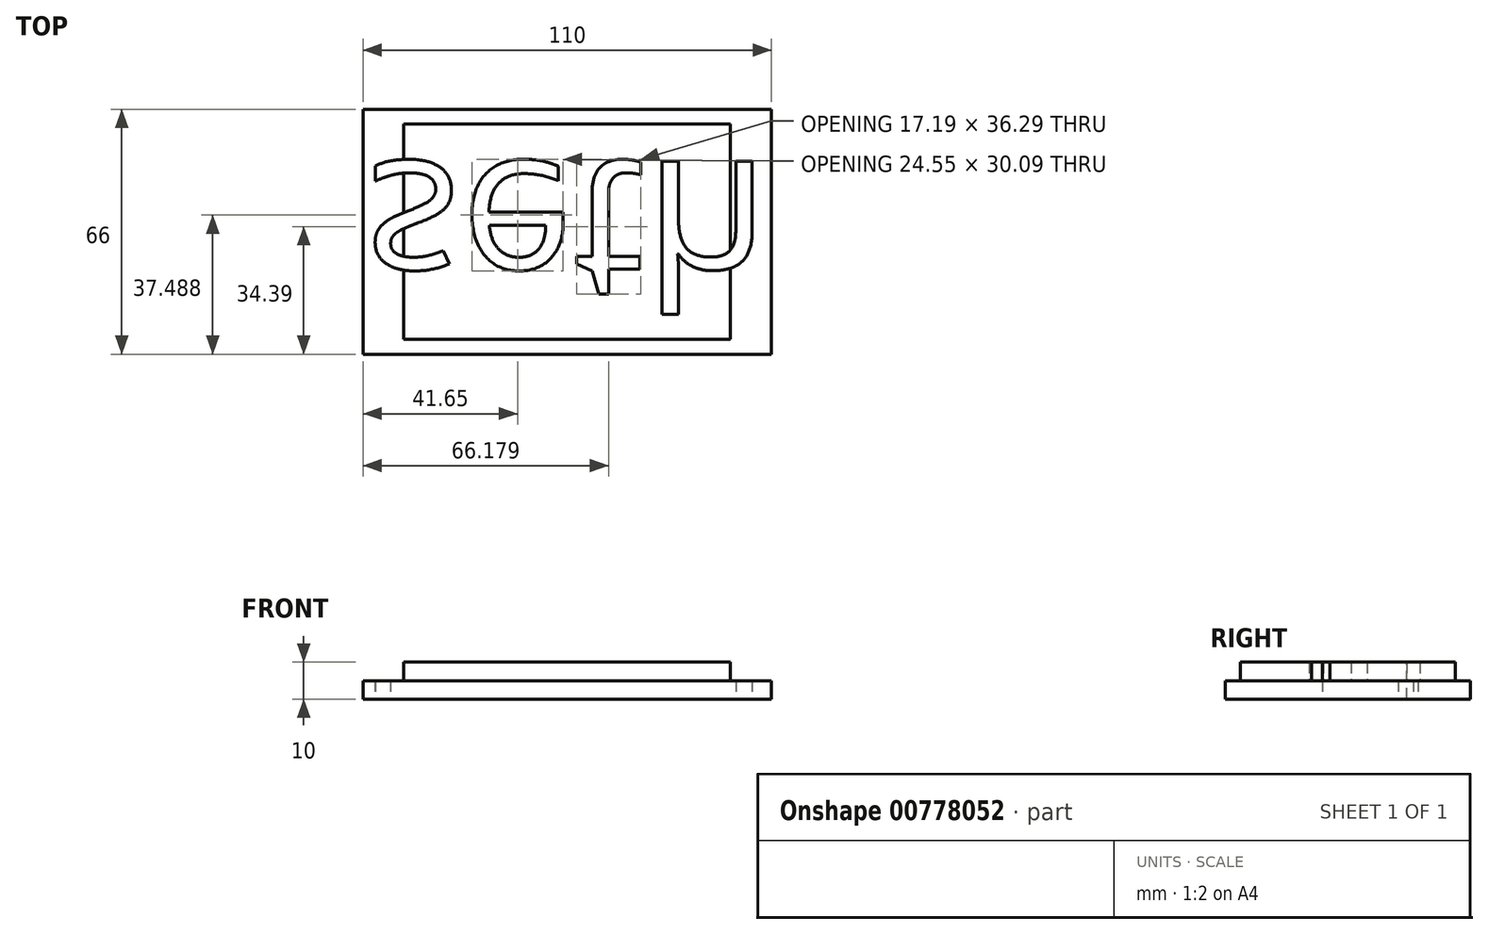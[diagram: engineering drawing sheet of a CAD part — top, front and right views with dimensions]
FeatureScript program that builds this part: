
annotation { "Feature Type Name" : "Feature", "Feature Type Description" : "" }
export const myFeature = defineFeature(function(context is Context, id is Id, definition is map)
    precondition{}
    {
        {
            var Q0;
            Q0=qCreatedBy(makeId("Top.planeOp"),FACE);
            var sketch = newSketch(context, id + "F0", { "sketchPlane" : qUnion([Q0])});
            skLineSegment(sketch, "E0.bottom", {"start": v(55, 33) * mm, "end": v(-55, 33) * mm});
            skLineSegment(sketch, "E0.top", {"start": v(55, -33) * mm, "end": v(-55, -33) * mm});
            skLineSegment(sketch, "E0.left", {"start": v(55, 33) * mm, "end": v(55, -33) * mm});
            skLineSegment(sketch, "E0.right", {"start": v(-55, 33) * mm, "end": v(-55, -33) * mm});
            skPoint(sketch, "E0.middle", {"position": v(0, 0) * mm});
            skSolve(sketch);
        }
        {
            var Q0;
            Q0=makeQuery(id+"F0.imprint","IMPRINT",FACE,{"disambiguationData":[TD([[makeQuery(id+"F0.imprint","IMPRINT",EDGE,{"derivedFrom":sQuery(id+"F0.wireOp",EDGE,"E0.bottom")}),1.0]])]});
            extrude(context, id + "F1", {"entities" : qUnion([Q0]), "depth" : 5 * mm, "offsetDistance" : 25 * mm});
        }
        {
            var Q0;
            Q0=makeQuery(id+"F1.opExtrude","CAP_FACE",FACE,{"disambiguationData":[OSD([sQuery(id+"F0.wireOp",EDGE,"E0.bottom"),sQuery(id+"F0.wireOp",EDGE,"E0.top"),sQuery(id+"F0.wireOp",EDGE,"E0.left"),sQuery(id+"F0.wireOp",EDGE,"E0.right")])],"isStart":false});
            var sketch = newSketch(context, id + "F2", { "sketchPlane" : qUnion([Q0])});
            skLineSegment(sketch, "E1.bottom", {"start": v(44, 29) * mm, "end": v(-44, 29) * mm});
            skLineSegment(sketch, "E1.top", {"start": v(44, -29) * mm, "end": v(-44, -29) * mm});
            skLineSegment(sketch, "E1.left", {"start": v(44, 29) * mm, "end": v(44, -29) * mm});
            skLineSegment(sketch, "E1.right", {"start": v(-44, 29) * mm, "end": v(-44, -29) * mm});
            skPoint(sketch, "E1.middle", {"position": v(0, 0) * mm});
            skSolve(sketch);
        }
        {
            var Q0;
            Q0=makeQuery(id+"F2.imprint","IMPRINT",FACE,{"disambiguationData":[TD([[makeQuery(id+"F2.imprint","IMPRINT",EDGE,{"derivedFrom":sQuery(id+"F2.wireOp",EDGE,"E1.bottom")}),1.0]])]});
            extrude(context, id + "F3", {"entities" : qUnion([Q0]), "operationType" : NewBodyOperationType.ADD, "depth" : 5 * mm, "offsetDistance" : 25 * mm});
        }
        {
            var Q0;
            Q0=makeQuery(id+"F1.opExtrude","CAP_FACE",FACE,{"disambiguationData":[OSD([sQuery(id+"F0.wireOp",EDGE,"E0.bottom"),sQuery(id+"F0.wireOp",EDGE,"E0.top"),sQuery(id+"F0.wireOp",EDGE,"E0.left"),sQuery(id+"F0.wireOp",EDGE,"E0.right")])],"isStart":true});
            var sketch = newSketch(context, id + "F4", { "sketchPlane" : qUnion([Q0])});
            skText(sketch, "E2", { "text": "seth", "fontName": "OpenSans-Regular.ttf"});
            const initialGuessF4  = {"E2": [-0.05454, -0.019, 1, 0, 0.03905]};
            skSetInitialGuess(sketch, initialGuessF4);
            skSolve(sketch);
        }
        {
            var Q0;
            Q0 = qSketchRegion(id + "F4", true);
            extrude(context, id + "F5", {"entities" : qUnion([Q0]), "operationType" : NewBodyOperationType.REMOVE, "oppositeDirection" : true, "depth" : 50 * mm, "offsetDistance" : 25 * mm});
        }
    });
